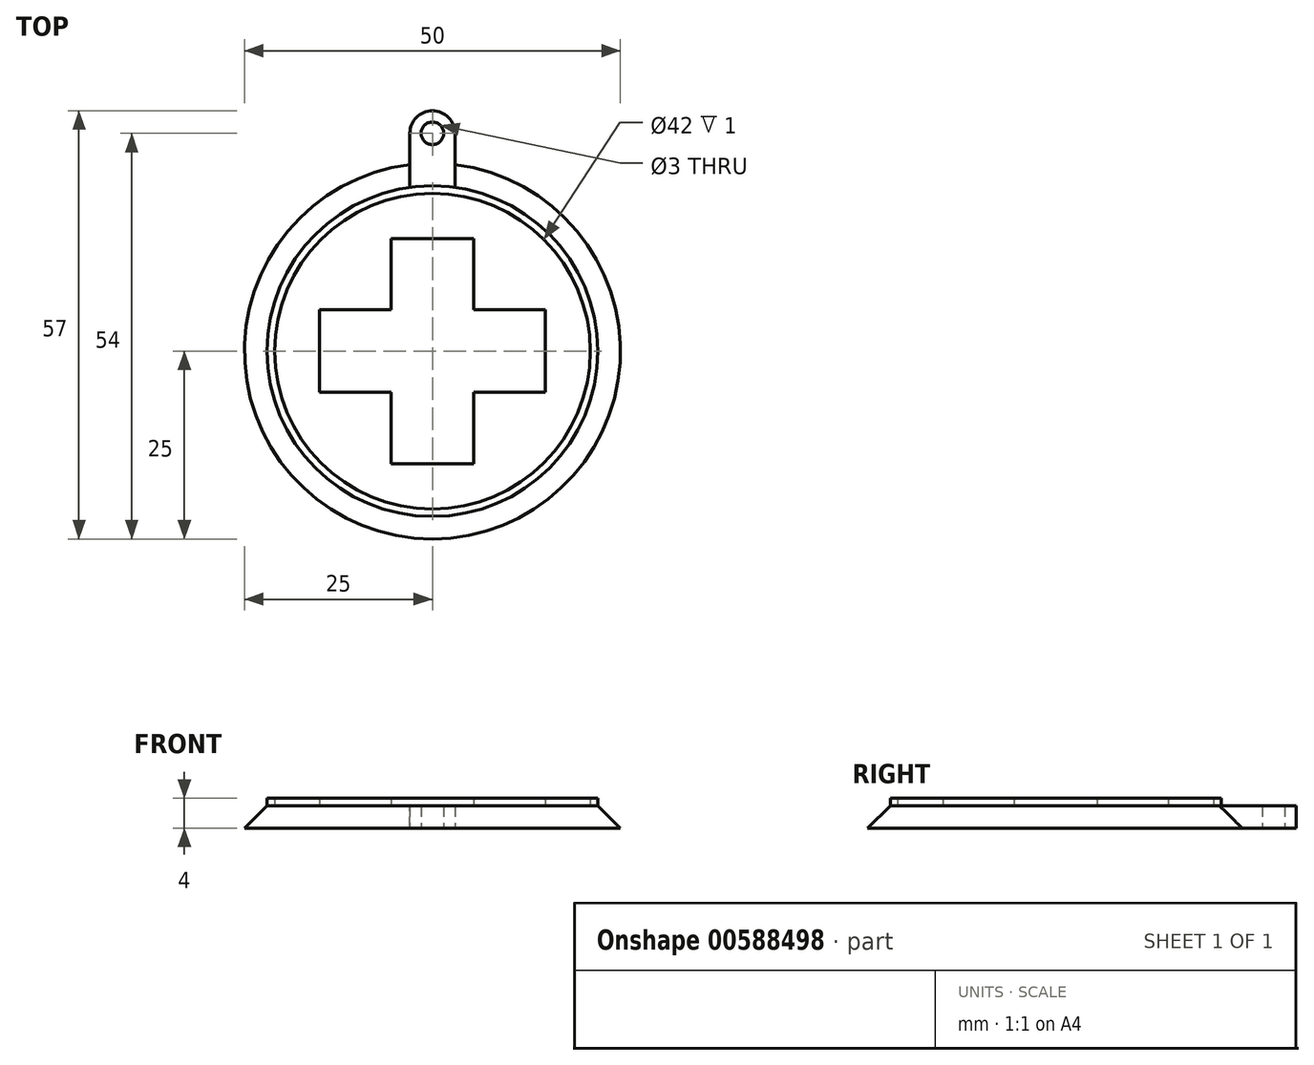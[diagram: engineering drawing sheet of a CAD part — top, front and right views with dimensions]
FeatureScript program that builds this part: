
annotation { "Feature Type Name" : "Feature", "Feature Type Description" : "" }
export const myFeature = defineFeature(function(context is Context, id is Id, definition is map)
    precondition{}
    {
        {
            var Q0;
            Q0=qCreatedBy(makeId("Top.planeOp"),FACE);
            var sketch = newSketch(context, id + "F0", { "sketchPlane" : qUnion([Q0])});
            skCircle(sketch, "E0", {"center": v(0, 0) * mm, "radius": 25 * mm});
            skSolve(sketch);
        }
        {
            var Q0;
            Q0=makeQuery(id+"F0.imprint","IMPRINT",FACE,{"disambiguationData":[TD([[makeQuery(id+"F0.imprint","IMPRINT",EDGE,{"derivedFrom":sQuery(id+"F0.wireOp",EDGE,"E0")}),1.0]])]});
            extrude(context, id + "F1", {"entities" : qUnion([Q0]), "depth" : 3 * mm, "offsetDistance" : 25 * mm});
        }
        {
            var Q0;
            Q0=makeQuery(id+"F1.opExtrude","CAP_FACE",FACE,{"disambiguationData":[OSD([sQuery(id+"F0.wireOp",EDGE,"E0")])],"isStart":false});
            var sketch = newSketch(context, id + "F2", { "sketchPlane" : qUnion([Q0])});
            skCircle(sketch, "E1", {"center": v(0, 0) * mm, "radius": 22 * mm});
            skCircle(sketch, "E2", {"center": v(0, 0) * mm, "radius": 21 * mm});
            skLineSegment(sketch, "E3.bottom", {"start": v(5.5, 15) * mm, "end": v(-5.5, 15) * mm});
            skLineSegment(sketch, "E3.top", {"start": v(5.5, -15) * mm, "end": v(-5.5, -15) * mm});
            skLineSegment(sketch, "E3.left", {"start": v(5.5, 15) * mm, "end": v(5.5, -15) * mm});
            skLineSegment(sketch, "E3.right", {"start": v(-5.5, 15) * mm, "end": v(-5.5, -15) * mm});
            skLineSegment(sketch, "E4.bottom", {"start": v(15, -5.5) * mm, "end": v(-15, -5.5) * mm});
            skLineSegment(sketch, "E4.top", {"start": v(15, 5.5) * mm, "end": v(-15, 5.5) * mm});
            skLineSegment(sketch, "E4.left", {"start": v(15, -5.5) * mm, "end": v(15, 5.5) * mm});
            skLineSegment(sketch, "E4.right", {"start": v(-15, -5.5) * mm, "end": v(-15, 5.5) * mm});
            skSolve(sketch);
        }
        {
            var Q0;
            {var subQ0=sQuery(id+"F2.wireOp",EDGE,"E4.top");var subQ1=sQuery(id+"F2.wireOp",EDGE,"E3.left");var subQ2=makeQuery(id+"F2.imprint","INTERSECT",VERTEX,{"derivedFrom":[subQ1,subQ0]});Q0=makeQuery(id+"F2.imprint","IMPRINT",FACE,{"disambiguationData":[TD([[makeQuery(id+"F2.imprint","IMPRINT",EDGE,{"disambiguationData":[TD([[subQ2,-1.0]])],"derivedFrom":subQ1}),-1.0]])]});}
            var Q1;
            {var subQ0=sQuery(id+"F2.wireOp",EDGE,"E3.bottom");Q1=makeQuery(id+"F2.imprint","IMPRINT",FACE,{"disambiguationData":[TD([[makeQuery(id+"F2.imprint","IMPRINT",EDGE,{"derivedFrom":subQ0}),1.0]])]});}
            var Q2;
            {var subQ5=sQuery(id+"F2.wireOp",EDGE,"E4.right");Q2=makeQuery(id+"F2.imprint","IMPRINT",FACE,{"disambiguationData":[TD([[makeQuery(id+"F2.imprint","IMPRINT",EDGE,{"derivedFrom":subQ5}),-1.0]])]});}
            var Q3;
            {var subQ0=sQuery(id+"F2.wireOp",EDGE,"E3.top");Q3=makeQuery(id+"F2.imprint","IMPRINT",FACE,{"disambiguationData":[TD([[makeQuery(id+"F2.imprint","IMPRINT",EDGE,{"derivedFrom":subQ0}),-1.0]])]});}
            var Q4;
            {var subQ5=sQuery(id+"F2.wireOp",EDGE,"E4.left");Q4=makeQuery(id+"F2.imprint","IMPRINT",FACE,{"disambiguationData":[TD([[makeQuery(id+"F2.imprint","IMPRINT",EDGE,{"derivedFrom":subQ5}),1.0]])]});}
            var Q5;
            Q5=makeQuery(id+"F2.imprint","IMPRINT",FACE,{"disambiguationData":[TD([[makeQuery(id+"F2.imprint","IMPRINT",EDGE,{"derivedFrom":sQuery(id+"F2.wireOp",EDGE,"E1")}),1.0]])]});
            extrude(context, id + "F3", {"entities" : qUnion([Q0, Q1, Q2, Q3, Q4, Q5]), "depth" : 1 * mm, "offsetDistance" : 25 * mm});
        }
        {
            var Q0;
            Q0=qCreatedBy(makeId("Top.planeOp"),FACE);
            var sketch = newSketch(context, id + "F4", { "sketchPlane" : qUnion([Q0])});
            skCircle(sketch, "E5", {"center": v(0, 29) * mm, "radius": 3 * mm});
            skCircle(sketch, "E6", {"center": v(0, 29) * mm, "radius": 1.5 * mm});
            skCircle(sketch, "E7.0", {"center": v(0, 0) * mm, "radius": 25 * mm});
            skLineSegment(sketch, "E8", {"start": v(-3, 29) * mm, "end": v(-3, 24.82) * mm});
            skLineSegment(sketch, "E9", {"start": v(3, 29) * mm, "end": v(3, 24.82) * mm});
            skSolve(sketch);
        }
        {
            var Q0;
            {var subQ0=sQuery(id+"F4.wireOp",EDGE,"E8");Q0=makeQuery(id+"F4.imprint","IMPRINT",FACE,{"disambiguationData":[TD([[makeQuery(id+"F4.imprint","IMPRINT",EDGE,{"derivedFrom":subQ0}),1.0]])]});}
            var Q1;
            Q1=makeQuery(id+"F4.imprint","IMPRINT",FACE,{"disambiguationData":[TD([[makeQuery(id+"F4.imprint","IMPRINT",EDGE,{"derivedFrom":sQuery(id+"F4.wireOp",EDGE,"E6")}),-1.0]])]});
            var Q2;
            Q2=makeQuery(id+"F1.opExtrude","CAP_FACE",FACE,{"disambiguationData":[OSD([sQuery(id+"F0.wireOp",EDGE,"E0")])],"isStart":false});
            extrude(context, id + "F5", {"entities" : qUnion([Q0, Q1]), "operationType" : NewBodyOperationType.ADD, "endBound" : BoundingType.UP_TO_SURFACE, "depth" : 25 * mm, "endBoundEntityFace" : qUnion([Q2]), "offsetDistance" : 25 * mm});
        }
        {
            var Q0;
            Q0=makeQuery(id+"F1.opExtrude","CAP_EDGE",EDGE,{"disambiguationData":[OSD([sQuery(id+"F0.wireOp",EDGE,"E0")])],"isStart":false});
            chamfer(context, id + "F6", {"entities" : qUnion([Q0]), "width" : 3 * mm, "tangentPropagation" : true});
        }
    });
